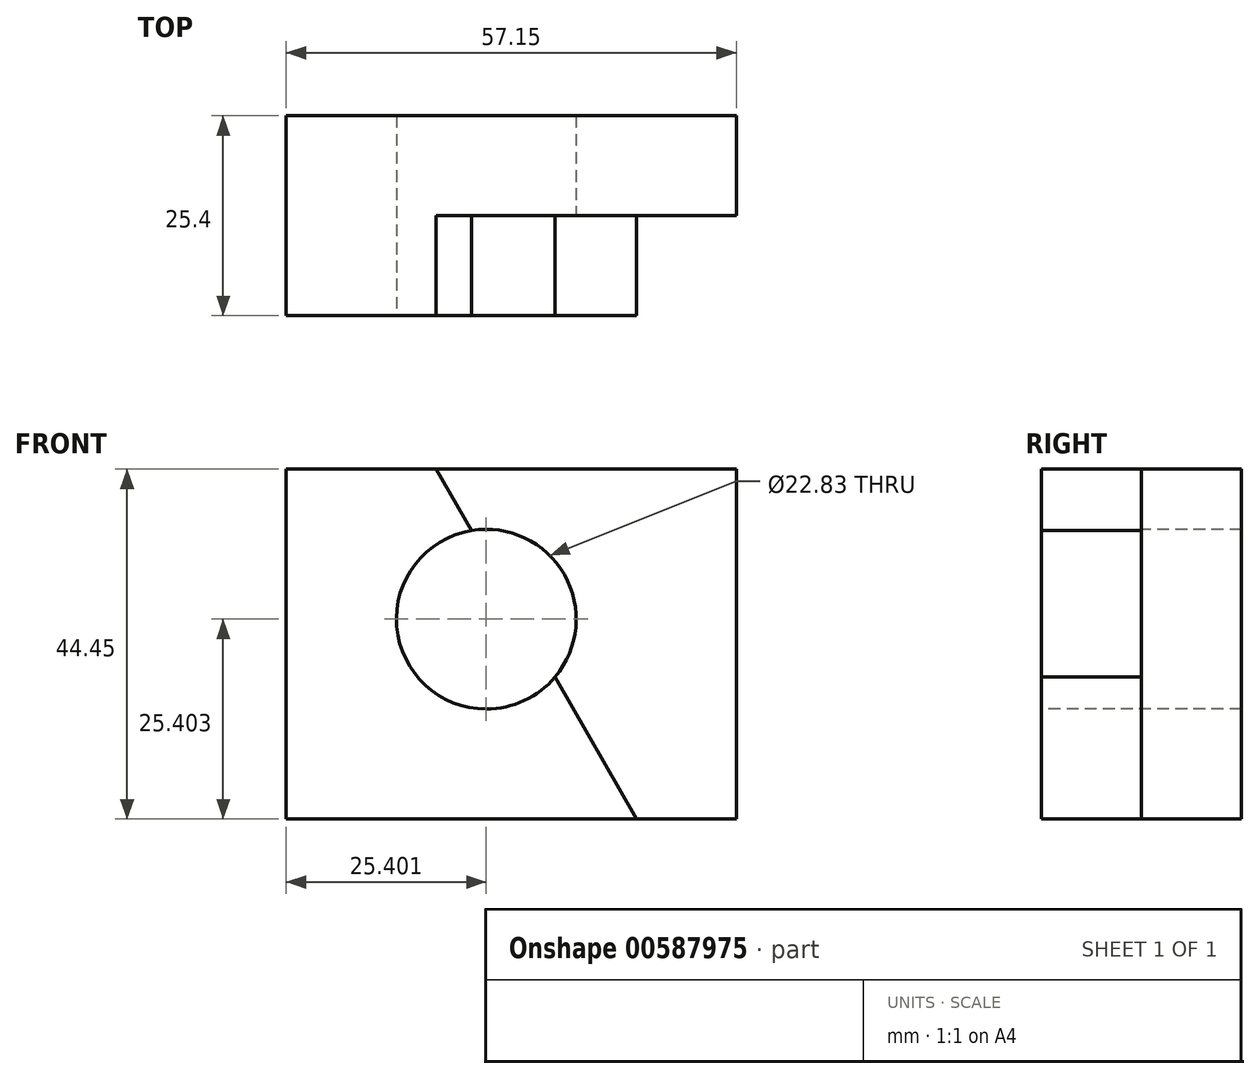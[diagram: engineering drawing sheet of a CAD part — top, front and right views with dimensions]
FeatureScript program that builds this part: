
annotation { "Feature Type Name" : "Feature", "Feature Type Description" : "" }
export const myFeature = defineFeature(function(context is Context, id is Id, definition is map)
    precondition{}
    {
        {
            var Q0;
            Q0=qCreatedBy(makeId("Front.planeOp"),FACE);
            var sketch = newSketch(context, id + "F0", { "sketchPlane" : qUnion([Q0])});
            skLineSegment(sketch, "E0.bottom", {"start": v(-53.5, 30.97) * mm, "end": v(3.65, 30.97) * mm});
            skLineSegment(sketch, "E0.top", {"start": v(-53.5, -13.48) * mm, "end": v(3.65, -13.48) * mm});
            skLineSegment(sketch, "E0.left", {"start": v(-53.5, 30.97) * mm, "end": v(-53.5, -13.48) * mm});
            skLineSegment(sketch, "E0.right", {"start": v(3.65, 30.97) * mm, "end": v(3.65, -13.48) * mm});
            skSolve(sketch);
        }
        {
            var Q0;
            Q0 = qSketchRegion(id + "F0", true);
            extrude(context, id + "F1", {"entities" : qUnion([Q0]), "depth" : 25.4 * mm, "offsetDistance" : 25.4 * mm});
        }
        {
            var Q0;
            Q0=makeQuery(id+"F1.opExtrude","CAP_FACE",FACE,{"disambiguationData":[OSD([sQuery(id+"F0.wireOp",EDGE,"E0.bottom"),sQuery(id+"F0.wireOp",EDGE,"E0.top"),sQuery(id+"F0.wireOp",EDGE,"E0.left"),sQuery(id+"F0.wireOp",EDGE,"E0.right")])],"isStart":false});
            var sketch = newSketch(context, id + "F2", { "sketchPlane" : qUnion([Q0])});
            skCircle(sketch, "E1", {"center": v(-28.1, 11.92) * mm, "radius": 11.41 * mm});
            skSolve(sketch);
        }
        {
            var Q0;
            Q0 = qSketchRegion(id + "F2", true);
            extrude(context, id + "F3", {"entities" : qUnion([Q0]), "operationType" : NewBodyOperationType.REMOVE, "oppositeDirection" : true, "depth" : 25.4 * mm, "offsetDistance" : 25.4 * mm});
        }
        {
            var Q0;
            Q0=makeQuery(id+"F1.opExtrude","CAP_FACE",FACE,{"disambiguationData":[OSD([sQuery(id+"F0.wireOp",EDGE,"E0.bottom"),sQuery(id+"F0.wireOp",EDGE,"E0.top"),sQuery(id+"F0.wireOp",EDGE,"E0.left"),sQuery(id+"F0.wireOp",EDGE,"E0.right")])],"isStart":false});
            var sketch = newSketch(context, id + "F4", { "sketchPlane" : qUnion([Q0])});
            skLineSegment(sketch, "E2", {"start": v(-34.45, 30.97) * mm, "end": v(-9.05, -13.48) * mm});
            skLineSegment(sketch, "E3", {"start": v(-9.05, -13.48) * mm, "end": v(3.65, -13.48) * mm});
            skLineSegment(sketch, "E4", {"start": v(3.65, -13.48) * mm, "end": v(3.65, 30.97) * mm});
            skLineSegment(sketch, "E5", {"start": v(3.65, 30.97) * mm, "end": v(-34.45, 30.97) * mm});
            skSolve(sketch);
        }
        {
            var Q0;
            Q0 = qSketchRegion(id + "F4", true);
            extrude(context, id + "F5", {"entities" : qUnion([Q0]), "operationType" : NewBodyOperationType.REMOVE, "oppositeDirection" : true, "depth" : 12.7 * mm, "offsetDistance" : 25.4 * mm});
        }
    });
